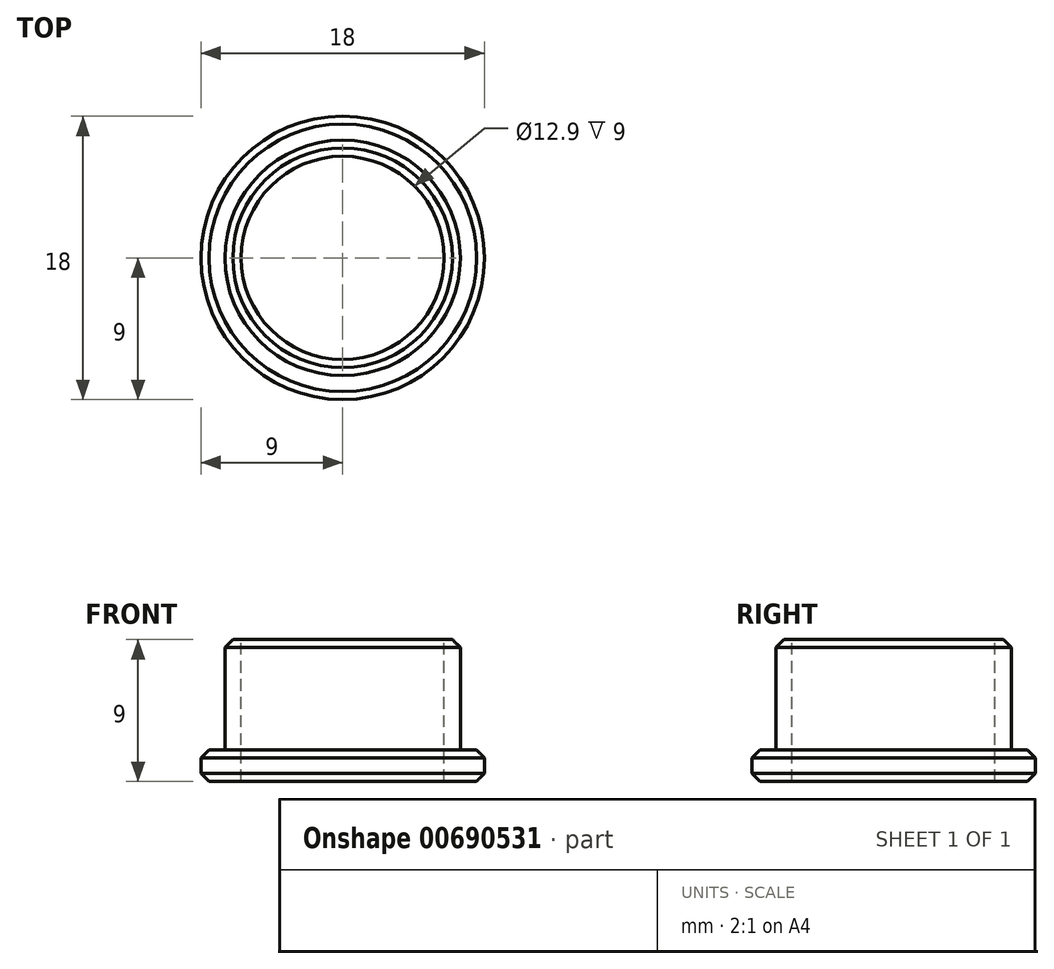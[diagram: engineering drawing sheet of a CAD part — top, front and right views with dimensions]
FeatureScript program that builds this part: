
annotation { "Feature Type Name" : "Feature", "Feature Type Description" : "" }
export const myFeature = defineFeature(function(context is Context, id is Id, definition is map)
    precondition{}
    {
        {
            var Q0;
            Q0=qCreatedBy(makeId("Top.planeOp"),FACE);
            var sketch = newSketch(context, id + "F0", { "sketchPlane" : qUnion([Q0])});
            skCircle(sketch, "E0", {"center": v(0, 0) * mm, "radius": 9 * mm});
            skSolve(sketch);
        }
        {
            var Q0;
            Q0=qSketchRegion(id+"F0",true);
            extrude(context, id + "F1", {"entities" : qUnion([Q0]), "depth" : 2 * mm, "offsetDistance" : 25 * mm});
        }
        {
            var Q0;
            Q0=makeQuery(id+"F1.opExtrude","CAP_FACE",FACE,{"disambiguationData":[OSD([sQuery(id+"F0.wireOp",EDGE,"E0")])],"isStart":false});
            var sketch = newSketch(context, id + "F2", { "sketchPlane" : qUnion([Q0])});
            skCircle(sketch, "E1", {"center": v(0, 0) * mm, "radius": 7.48 * mm});
            skSolve(sketch);
        }
        {
            var Q0;
            Q0=makeQuery(id+"F2.imprint","IMPRINT",FACE,{"disambiguationData":[TD([[makeQuery(id+"F2.imprint","IMPRINT",EDGE,{"derivedFrom":sQuery(id+"F2.wireOp",EDGE,"E1")}),1.0]])]});
            extrude(context, id + "F3", {"entities" : qUnion([Q0]), "operationType" : NewBodyOperationType.ADD, "depth" : 7 * mm, "offsetDistance" : 25 * mm});
        }
        {
            var Q0;
            Q0=makeQuery(id+"F3.opExtrude","CAP_FACE",FACE,{"disambiguationData":[OSD([sQuery(id+"F2.wireOp",EDGE,"E1")])],"isStart":false});
            var sketch = newSketch(context, id + "F4", { "sketchPlane" : qUnion([Q0])});
            skCircle(sketch, "E2", {"center": v(0, 0) * mm, "radius": 6.45 * mm});
            skSolve(sketch);
        }
        {
            var Q0;
            Q0=makeQuery(id+"F4.imprint","IMPRINT",FACE,{"disambiguationData":[TD([[makeQuery(id+"F4.imprint","IMPRINT",EDGE,{"derivedFrom":sQuery(id+"F4.wireOp",EDGE,"E2")}),1.0]])]});
            extrude(context, id + "F5", {"entities" : qUnion([Q0]), "operationType" : NewBodyOperationType.REMOVE, "oppositeDirection" : true, "depth" : 25 * mm, "offsetDistance" : 25 * mm});
        }
        {
            var Q0;
            Q0=makeQuery(id+"F3.opExtrude","CAP_EDGE",EDGE,{"disambiguationData":[OSD([sQuery(id+"F2.wireOp",EDGE,"E1")])],"isStart":false});
            var Q1;
            Q1=makeQuery(id+"F1.opExtrude","CAP_EDGE",EDGE,{"disambiguationData":[OSD([sQuery(id+"F0.wireOp",EDGE,"E0")])],"isStart":false});
            var Q2;
            Q2=makeQuery(id+"F1.opExtrude","CAP_EDGE",EDGE,{"disambiguationData":[OSD([sQuery(id+"F0.wireOp",EDGE,"E0")])],"isStart":true});
            var Q3;
            Q3=makeQuery(id+"F5.boolean.opBoolean","COPY",EDGE,{"derivedFrom":makeQuery(id+"F5.opExtrude","CAP_EDGE",EDGE,{"disambiguationData":[OSD([sQuery(id+"F4.wireOp",EDGE,"E2")])],"isStart":true})});
            chamfer(context, id + "F6", {"entities" : qUnion([Q0, Q1, Q2, Q3]), "width" : 0.5 * mm, "tangentPropagation" : true});
        }
    });
